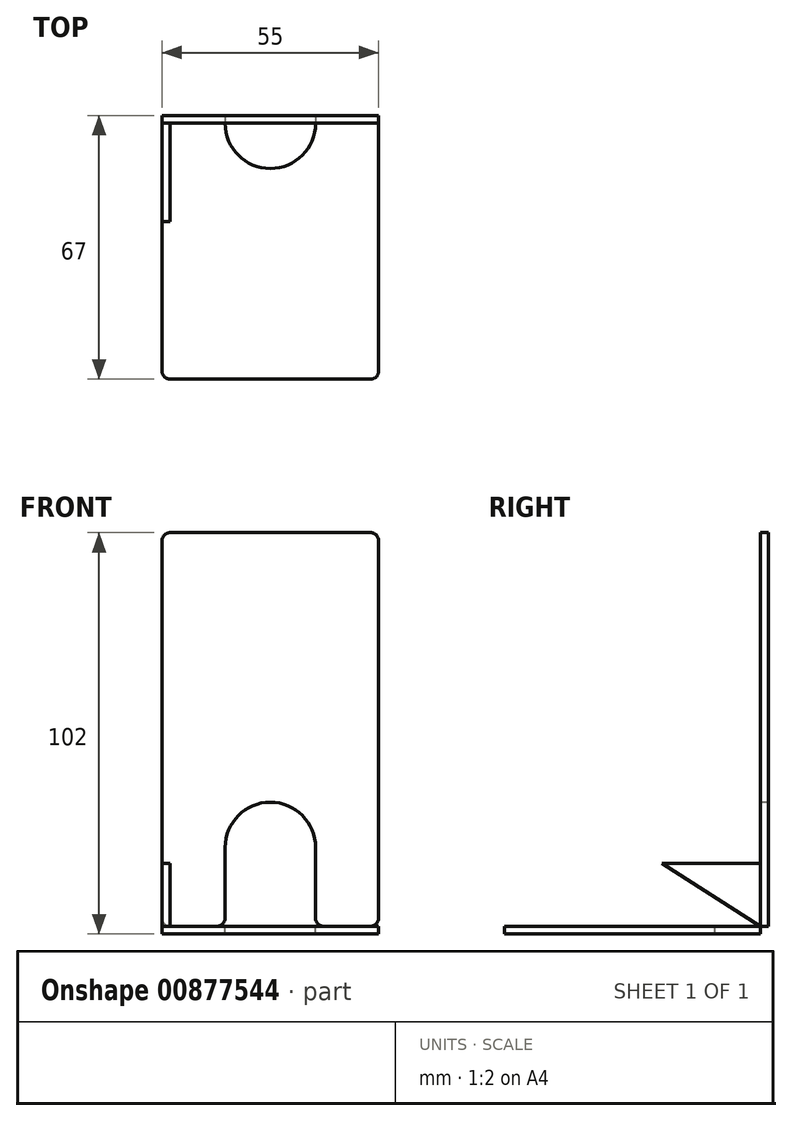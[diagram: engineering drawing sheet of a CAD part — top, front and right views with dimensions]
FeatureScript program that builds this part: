
annotation { "Feature Type Name" : "Feature", "Feature Type Description" : "" }
export const myFeature = defineFeature(function(context is Context, id is Id, definition is map)
    precondition{}
    {
        {
            var Q0;
            Q0=qCreatedBy(makeId("Front.planeOp"),FACE);
            var sketch = newSketch(context, id + "F0", { "sketchPlane" : qUnion([Q0])});
            skLineSegment(sketch, "E0.bottom", {"start": v(0, 0) * mm, "end": v(55, 0) * mm});
            skLineSegment(sketch, "E0.top", {"start": v(0, 100) * mm, "end": v(55, 100) * mm});
            skLineSegment(sketch, "E0.left", {"start": v(0, 0) * mm, "end": v(0, 100) * mm});
            skLineSegment(sketch, "E0.right", {"start": v(55, 0) * mm, "end": v(55, 100) * mm});
            skLineSegment(sketch, "E1", {"start": v(0, 0) * mm, "end": v(16, 0) * mm});
            skLineSegment(sketch, "E2", {"start": v(16, 0) * mm, "end": v(16, 20) * mm});
            skLineSegment(sketch, "E3", {"start": v(55, 0) * mm, "end": v(39, 0) * mm});
            skLineSegment(sketch, "E4", {"start": v(39, 0) * mm, "end": v(39, 20) * mm});
            skArc(sketch, "E5", {"start": v(16, 20) * mm, "mid": v(27.5, 31.5) * mm, "end": v(39, 20) * mm});
            skSolve(sketch);
        }
        {
            var Q0;
            Q0=makeQuery(id+"F0.imprint","IMPRINT",FACE,{"disambiguationData":[TD([[makeQuery(id+"F0.imprint","IMPRINT",EDGE,{"derivedFrom":sQuery(id+"F0.wireOp",EDGE,"E0.top")}),-1.0]])]});
            extrude(context, id + "F1", {"entities" : qUnion([Q0]), "depth" : -2 * mm, "offsetDistance" : 25 * mm});
        }
        {
            var Q0;
            Q0=makeQuery(id+"F1.opExtrude","SWEPT_EDGE",EDGE,{"disambiguationData":[OSD([sQuery(id+"F0.wireOp",EDGE,"E0.top"),sQuery(id+"F0.wireOp",EDGE,"E0.left")])]});
            var Q1;
            Q1=makeQuery(id+"F1.opExtrude","SWEPT_EDGE",EDGE,{"disambiguationData":[OSD([sQuery(id+"F0.wireOp",EDGE,"E0.top"),sQuery(id+"F0.wireOp",EDGE,"E0.right")])]});
            var Q2;
            Q2=makeQuery(id+"F1.opExtrude","SWEPT_EDGE",EDGE,{"disambiguationData":[OSD([sQuery(id+"F0.wireOp",EDGE,"E0.right"),sQuery(id+"F0.wireOp",EDGE,"E3")])]});
            var Q3;
            Q3=makeQuery(id+"F1.opExtrude","SWEPT_EDGE",EDGE,{"disambiguationData":[OSD([sQuery(id+"F0.wireOp",EDGE,"E0.bottom"),sQuery(id+"F0.wireOp",EDGE,"E3"),sQuery(id+"F0.wireOp",EDGE,"E4")])]});
            var Q4;
            Q4=makeQuery(id+"F1.opExtrude","SWEPT_EDGE",EDGE,{"disambiguationData":[OSD([sQuery(id+"F0.wireOp",EDGE,"E0.bottom"),sQuery(id+"F0.wireOp",EDGE,"E1"),sQuery(id+"F0.wireOp",EDGE,"E2")])]});
            var Q5;
            Q5=makeQuery(id+"F1.opExtrude","SWEPT_EDGE",EDGE,{"disambiguationData":[OSD([sQuery(id+"F0.wireOp",EDGE,"E0.left"),sQuery(id+"F0.wireOp",EDGE,"E1")])]});
            fillet(context, id + "F2", {"entities" : qUnion([Q0, Q1, Q2, Q3, Q4, Q5]), "radius" : 2 * mm, "tangentPropagation" : true, "allowEdgeOverflow" : false});
        }
        {
            var Q0;
            Q0=qCreatedBy(makeId("Top.planeOp"),FACE);
            var sketch = newSketch(context, id + "F3", { "sketchPlane" : qUnion([Q0])});
            skLineSegment(sketch, "E6.bottom", {"start": v(0, 0) * mm, "end": v(55, 0) * mm});
            skLineSegment(sketch, "E6.top", {"start": v(0, -65) * mm, "end": v(55, -65) * mm});
            skLineSegment(sketch, "E6.left", {"start": v(0, 0) * mm, "end": v(0, -65) * mm});
            skLineSegment(sketch, "E6.right", {"start": v(55, 0) * mm, "end": v(55, -65) * mm});
            skLineSegment(sketch, "E7", {"start": v(0, 0) * mm, "end": v(16, 0) * mm});
            skLineSegment(sketch, "E8", {"start": v(16, 0) * mm, "end": v(39, 0) * mm});
            skLineSegment(sketch, "E9", {"start": v(39, 0) * mm, "end": v(55, 0) * mm});
            skLineSegment(sketch, "E10", {"start": v(16, 0) * mm, "end": v(16, 0) * mm});
            skLineSegment(sketch, "E11", {"start": v(27.5, -11.5) * mm, "end": v(27.5, -11.5) * mm});
            skLineSegment(sketch, "E12.bottom", {"start": v(39, -11.5) * mm, "end": v(39, -11.5) * mm});
            skLineSegment(sketch, "E12.top", {"start": v(39, 0) * mm, "end": v(39, 0) * mm});
            skLineSegment(sketch, "E12.right", {"start": v(39, 0) * mm, "end": v(39, 0) * mm});
            skPoint(sketch, "E13.visualSharp", {"position": v(16, -11.5) * mm});
            skArc(sketch, "E13.filletArc", {"start": v(16, 0) * mm, "mid": v(19.37, -8.13) * mm, "end": v(27.5, -11.5) * mm});
            skPoint(sketch, "E14.visualSharp", {"position": v(39, -11.5) * mm});
            skArc(sketch, "E14.filletArc", {"start": v(27.5, -11.5) * mm, "mid": v(35.63, -8.13) * mm, "end": v(39, 0) * mm});
            skSolve(sketch);
        }
        {
            var Q0;
            Q0=makeQuery(id+"F3.imprint","IMPRINT",FACE,{"disambiguationData":[TD([[makeQuery(id+"F3.imprint","IMPRINT",EDGE,{"derivedFrom":sQuery(id+"F3.wireOp",EDGE,"E6.top")}),1.0]])]});
            extrude(context, id + "F4", {"entities" : qUnion([Q0]), "depth" : -2 * mm, "offsetDistance" : 25 * mm});
        }
        {
            var Q0;
            Q0=makeQuery(id+"F4.opExtrude","SWEPT_EDGE",EDGE,{"disambiguationData":[OSD([sQuery(id+"F3.wireOp",EDGE,"E6.top"),sQuery(id+"F3.wireOp",EDGE,"E6.left")])]});
            var Q1;
            Q1=makeQuery(id+"F4.opExtrude","SWEPT_EDGE",EDGE,{"disambiguationData":[OSD([sQuery(id+"F3.wireOp",EDGE,"E6.top"),sQuery(id+"F3.wireOp",EDGE,"E6.right")])]});
            fillet(context, id + "F5", {"entities" : qUnion([Q0, Q1]), "radius" : 2 * mm, "tangentPropagation" : true, "allowEdgeOverflow" : false});
        }
        {
            var Q0;
            Q0=qCreatedBy(makeId("Right.planeOp"),FACE);
            var sketch = newSketch(context, id + "F6", { "sketchPlane" : qUnion([Q0])});
            skLineSegment(sketch, "E15", {"start": v(0, 0) * mm, "end": v(0, 16) * mm});
            skLineSegment(sketch, "E16", {"start": v(0, 16) * mm, "end": v(-25, 16) * mm});
            skLineSegment(sketch, "E17", {"start": v(-25, 16) * mm, "end": v(0, 0) * mm});
            skSolve(sketch);
        }
        {
            var Q0;
            Q0=makeQuery(id+"F6.imprint","IMPRINT",FACE,{"disambiguationData":[TD([[makeQuery(id+"F6.imprint","IMPRINT",EDGE,{"derivedFrom":sQuery(id+"F6.wireOp",EDGE,"E15")}),1.0]])]});
            extrude(context, id + "F7", {"entities" : qUnion([Q0]), "depth" : 2 * mm, "offsetDistance" : 25 * mm});
        }
    });
